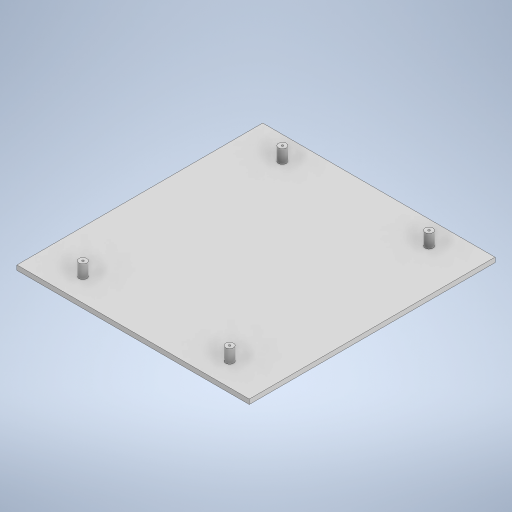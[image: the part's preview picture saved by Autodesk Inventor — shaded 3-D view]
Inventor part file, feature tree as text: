
AUTODESK INVENTOR PART (.ipt)
format: ipt  version: 2024.3 (Build 283343000, 343)  size: 244,224 bytes
history: native  units: mm
features: other x5, sketch x3, extrude x2, hole x1, pattern_circular x1, mirror x1
ambient origin geometry x8: Origin, YZ Plane, XZ Plane, XY Plane, X Axis, Y Axis, Z Axis, Center Point
bodies: Body1 (feature_tree)
feature tree (13):
  other  "Těleso1"
  extrude  "Vysunutí1"  Depth=183.0mm
  extrude  "Vysunutí2"  Depth=173.0mm
  other  "Pracovní rovina1"
  other  "Pracovní rovina2"
  hole  "Díra1"  [1 undecoded]
  pattern_circular  "Kruhové pole1"  [2 undecoded]
  mirror  "Zrcadlit1"
  other  "Pracovní rovina5"
  sketch  "Náčrt1"
  sketch  "Náčrt2"
  sketch  "Náčrt3"
  other  "Pracovní rovina3"
note: 3 required parameter values undecoded (feature->parameter linkage not recoverable at this tier; creation-order binding heuristic only, values carry confidence <= 0.55)
